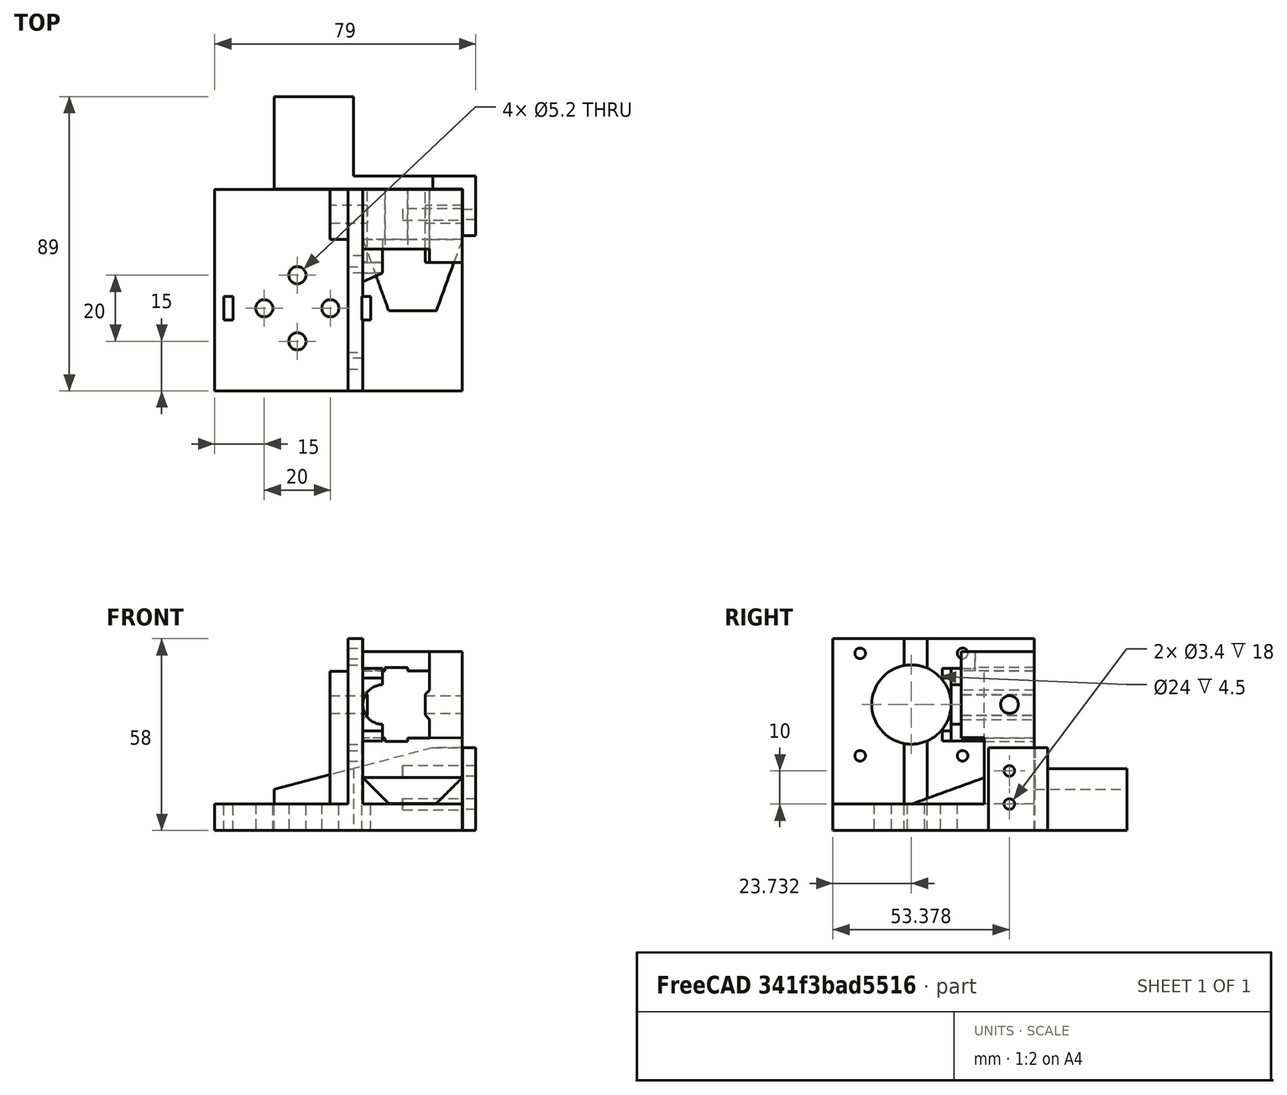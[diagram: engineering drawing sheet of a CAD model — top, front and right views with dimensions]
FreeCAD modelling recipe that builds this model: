
FCSTD DOCUMENT  (FreeCAD 1.0R39109 (Git))
Label: plotter_x_axis
License: All rights reserved
LicenseURL: https://en.wikipedia.org/wiki/All_rights_reserved
objects: Sketcher::SketchObject×20, PartDesign::Pad×17, PartDesign::Pocket×7, Mesh::Feature×2, PartDesign::Body×2, PartDesign::LinearPattern×1
note: 116 computed .brp shape members not serialized (recipe doc carries the construction recipe); baked Part::Feature solids carry a one-line shape summary decoded from their .brp

FEATURE [Mesh::Feature] _0x20_v_slot  label="20x20_v-slot"
  Placement = pos=(29.9,14,38) rot=(0,0,1;0rad)
FEATURE [Mesh::Feature] Motor_NEMA17
  Placement = pos=(-1.8,-1.5,38) rot=(0,1,0;1.5708rad)
FEATURE [Sketcher::SketchObject] Sketch007
  ArcFitTolerance = 1e-06
  AttachmentSupport = -> [XY_Plane001]
  FullyConstrained = false
  MakeInternals = false
  MapMode = 5
  sketch-geometry (19):
    g0: LineSegment StartX=49.9144 StartY=35.9499 StartZ=0 EndX=-25 EndY=35.9499 EndZ=0
    g1: LineSegment StartX=-25 StartY=35.9499 StartZ=0 EndX=-25 EndY=-25 EndZ=0
    g2: LineSegment StartX=-25 StartY=-25 StartZ=0 EndX=49.9144 EndY=-25 EndZ=0
    g3: LineSegment StartX=49.9144 StartY=-25 StartZ=0 EndX=49.9144 EndY=35.9499 EndZ=0
    g4: Circle CenterX=0 CenterY=10 CenterZ=0 NormalX=0 NormalY=0 NormalZ=1 AngleXU=0 Radius=2.6
    g5: Circle CenterX=10 CenterY=0 CenterZ=0 NormalX=0 NormalY=0 NormalZ=1 AngleXU=0 Radius=2.6
    g6: Circle CenterX=-10 CenterY=0 CenterZ=0 NormalX=0 NormalY=0 NormalZ=1 AngleXU=0 Radius=2.6
    g7: Circle CenterX=0 CenterY=-10 CenterZ=0 NormalX=0 NormalY=0 NormalZ=1 AngleXU=0 Radius=2.6
    g8: LineSegment [constr] StartX=43.4104 StartY=34.4675 StartZ=0 EndX=43.4104 EndY=14.8633 EndZ=0
    g9: LineSegment StartX=22.25 StartY=-3.5 StartZ=0 EndX=22.25 EndY=3.5 EndZ=0
    g10: LineSegment StartX=22.25 StartY=3.5 StartZ=0 EndX=19.5 EndY=3.5 EndZ=0
    g11: LineSegment StartX=19.5 StartY=3.5 StartZ=0 EndX=19.5 EndY=-3.5 EndZ=0
    g12: LineSegment StartX=19.5 StartY=-3.5 StartZ=0 EndX=22.25 EndY=-3.5 EndZ=0
    g13: GeomPoint [constr] X=20.875 Y=0 Z=0
    g14: LineSegment StartX=-19.5 StartY=-3.5 StartZ=0 EndX=-19.5 EndY=3.5 EndZ=0
    g15: LineSegment StartX=-19.5 StartY=3.5 StartZ=0 EndX=-22.25 EndY=3.5 EndZ=0
    g16: LineSegment StartX=-22.25 StartY=3.5 StartZ=0 EndX=-22.25 EndY=-3.5 EndZ=0
    g17: LineSegment StartX=-22.25 StartY=-3.5 StartZ=0 EndX=-19.5 EndY=-3.5 EndZ=0
    g18: GeomPoint [constr] X=-20.875 Y=0 Z=0
  constraints (49):
    c: Coincident(g0,g1)
    c: Coincident(g1,g2)
    c: Coincident(g2,g3)
    c: Coincident(g3,g0)
    c: Horizontal(g0)
    c: Horizontal(g2)
    c: Vertical(g1)
    c: Vertical(g3)
    c: Diameter(g4) = 5.2
    c: PointOnObject(g4,g-2)
    c: Diameter(g5) = 5.2
    c: PointOnObject(g5,g-1)
    c: Diameter(g6) = 5.2
    c: Diameter(g7) = 5.2
    c: PointOnObject(g7,g-2)
    c: DistanceX(g-1,g5) = 10
    c: DistanceY(g7,g-1) = 10
    c: DistanceY(g-1,g4) = 10
    c: DistanceX(g6,g-1) = 10
    c: PointOnObject(g6,g-1)
    c: Vertical(g8)
    c: DistanceY(g1,g-1) = 25
    c: DistanceX(g1,g-1) = 25
    c: Coincident(g9,g10)
    c: Coincident(g10,g11)
    c: Coincident(g11,g12)
    c: Coincident(g12,g9)
    c: Vertical(g9)
    c: Vertical(g11)
    c: Horizontal(g10)
    c: Horizontal(g12)
    c: Symmetric(g11,g9,g13)
    c: PointOnObject(g13,g-1)
    c: Coincident(g14,g15)
    c: Coincident(g15,g16)
    c: Coincident(g16,g17)
    c: Coincident(g17,g14)
    c: Vertical(g14)
    c: Vertical(g16)
    c: Horizontal(g15)
    c: Horizontal(g17)
    c: Symmetric(g16,g14,g18)
    c: PointOnObject(g18,g-1)
    c: Equal(g11,g14)
    c: DistanceY(g11,g11) = 7
    c: Equal(g10,g15)
    c: DistanceX(g15,g15) = 2.75
    c: DistanceX(g14,g11) = 39
    c: DistanceX(g14,g-1) = 19.5
FEATURE [PartDesign::Pad] Pad005
  Direction = (0,0,1)
  Length = 8
  Length2 = 10
  Profile = -> Sketch007
  ReferenceAxis = -> Sketch007 [N_Axis]
  Refine = true
  Suppressed = false
  Type = 0
FEATURE [Sketcher::SketchObject] Sketch009
  ArcFitTolerance = 1e-06
  AttachmentSupport = -> [Pad005]
  ExternalGeometry = -> [Pad005]
  FullyConstrained = false
  MakeInternals = false
  MapMode = 5
  Placement = pos=(0,0,8) rot=(0,0,1;0rad)
  sketch-geometry (4):
    g0: LineSegment StartX=49.9144 StartY=35.9499 StartZ=0 EndX=9.91437 EndY=35.9499 EndZ=0
    g1: LineSegment StartX=9.91437 StartY=35.9499 StartZ=0 EndX=9.91437 EndY=20.8055 EndZ=0
    g2: LineSegment StartX=9.91437 StartY=20.8055 StartZ=0 EndX=49.9144 EndY=20.8055 EndZ=0
    g3: LineSegment StartX=49.9144 StartY=20.8055 StartZ=0 EndX=49.9144 EndY=35.9499 EndZ=0
  constraints (10):
    c: Coincident(g0,g1)
    c: Coincident(g1,g2)
    c: Coincident(g2,g3)
    c: Coincident(g3,g0)
    c: Horizontal(g0)
    c: Horizontal(g2)
    c: Vertical(g1)
    c: Vertical(g3)
    c: Distance(g1,g3) = 40
    c: Coincident(g0,g-4)
FEATURE [PartDesign::Pad] Pad006
  BaseFeature = -> Pad005
  Direction = (0,0,1)
  Length = 40.1
  Length2 = 10
  Profile = -> Sketch009
  ReferenceAxis = -> Sketch009 [N_Axis]
  Refine = true
  Suppressed = false
  Type = 0
FEATURE [Sketcher::SketchObject] Sketch010
  ArcFitTolerance = 1e-06
  AttachmentSupport = -> [Pad006]
  ExternalGeometry = -> [Pad006]
  FullyConstrained = false
  MakeInternals = false
  MapMode = 5
  Placement = pos=(0,20.8055,0) rot=(1,0,0;1.5708rad)
  sketch-geometry (17):
    g0: LineSegment [constr] StartX=29.9144 StartY=48.1 StartZ=0 EndX=29.9144 EndY=14.8286 EndZ=0
    g1: LineSegment StartX=19.8144 StartY=48.1 StartZ=0 EndX=19.8144 EndY=42.4266 EndZ=0
    g2: LineSegment StartX=19.8144 StartY=42.4266 StartZ=0 EndX=21.1404 EndY=41.0594 EndZ=0
    g3: LineSegment StartX=21.1404 StartY=41.0594 StartZ=0 EndX=21.1404 EndY=34.8594 EndZ=0
    g4: LineSegment StartX=21.1404 StartY=34.8594 StartZ=0 EndX=19.8144 EndY=33.5734 EndZ=0
    g5: LineSegment StartX=19.8144 StartY=33.5734 StartZ=0 EndX=19.8144 EndY=27.9 EndZ=0
    g6: LineSegment StartX=19.8144 StartY=27.9 StartZ=0 EndX=26.496 EndY=27.9 EndZ=0
    g7: LineSegment StartX=26.496 StartY=27.9 StartZ=0 EndX=26.496 EndY=26.9 EndZ=0
    g8: LineSegment StartX=26.496 StartY=26.9 StartZ=0 EndX=33.3327 EndY=26.9 EndZ=0
    g9: LineSegment StartX=33.3327 StartY=26.9 StartZ=0 EndX=33.3327 EndY=27.9 EndZ=0
    g10: LineSegment StartX=33.3327 StartY=27.9 StartZ=0 EndX=40.0144 EndY=27.9 EndZ=0
    g11: LineSegment StartX=40.0144 StartY=27.9 StartZ=0 EndX=40.0144 EndY=33.5734 EndZ=0
    g12: LineSegment StartX=40.0144 StartY=33.5734 StartZ=0 EndX=38.6893 EndY=34.9653 EndZ=0
    g13: LineSegment StartX=38.6893 StartY=34.9653 StartZ=0 EndX=38.6893 EndY=41.1653 EndZ=0
    g14: LineSegment StartX=38.6893 StartY=41.1653 StartZ=0 EndX=40.0144 EndY=42.4266 EndZ=0
    g15: LineSegment StartX=40.0144 StartY=42.4266 StartZ=0 EndX=40.0144 EndY=48.1 EndZ=0
    g16: LineSegment StartX=40.0144 StartY=48.1 StartZ=0 EndX=19.8144 EndY=48.1 EndZ=0
  constraints (46):
    c: Symmetric(g-3,g-3,g0)
    c: Vertical(g0)
    c: PointOnObject(g1,g-3)
    c: Vertical(g1)
    c: Coincident(g1,g2)
    c: Coincident(g2,g3)
    c: Vertical(g3)
    c: Coincident(g3,g4)
    c: Coincident(g4,g5)
    c: Vertical(g5)
    c: Coincident(g5,g6)
    c: Coincident(g6,g7)
    c: Vertical(g7)
    c: Coincident(g7,g8)
    c: Horizontal(g8)
    c: Coincident(g8,g9)
    c: Vertical(g9)
    c: Coincident(g9,g10)
    c: Coincident(g10,g11)
    c: Vertical(g11)
    c: Coincident(g11,g12)
    c: Coincident(g12,g13)
    c: Vertical(g13)
    c: Coincident(g13,g14)
    c: Coincident(g14,g15)
    c: PointOnObject(g15,g-3)
    c: Vertical(g15)
    c: Coincident(g15,g16)
    c: Coincident(g16,g1)
    c: Equal(g13,g3)
    c: Equal(g15,g1)
    c: Equal(g1,g5)
    c: Equal(g5,g11)
    c: Equal(g6,g10)
    c: Equal(g9,g7)
    c: DistanceY(g3,g3) = 6.2
    c: DistanceX(g4,g11) = 20.2
    c: DistanceX(g11,g14) = 0
    c: DistanceX(g1,g4) = 0
    c: DistanceY(g10,g15) = 20.2
    c: DistanceY(g10,g5) = 0
    c: Parallel(g6,g10)
    c: DistanceY(g9,g9) = 1
    c: DistanceX(g1,g0) = 10.1
    c: Perpendicular(g4,g2)
    c: Perpendicular(g12,g14)
FEATURE [PartDesign::Pocket] Pocket004
  BaseFeature = -> Pad006
  Direction = (0,1,-2e-16)
  Length = 50
  Length2 = 5
  Profile = -> Sketch010
  ReferenceAxis = -> Sketch010 [N_Axis]
  Refine = true
  Suppressed = false
  Type = 0
FEATURE [Sketcher::SketchObject] Sketch011
  ArcFitTolerance = 1e-06
  AttachmentSupport = -> [Pocket004]
  ExternalGeometry = -> [Pocket004]
  FullyConstrained = true
  MakeInternals = false
  MapMode = 5
  Placement = pos=(0,0,8) rot=(0,0,1;0rad)
  sketch-geometry (8):
    g0: LineSegment StartX=15.3144 StartY=20.8055 StartZ=0 EndX=15.3144 EndY=-25 EndZ=0
    g1: LineSegment StartX=15.3144 StartY=-25 StartZ=0 EndX=19.8144 EndY=-25 EndZ=0
    g2: LineSegment StartX=19.8144 StartY=-25 StartZ=0 EndX=19.8144 EndY=-3.5 EndZ=0
    g3: LineSegment StartX=19.8144 StartY=-3.5 StartZ=0 EndX=19.5 EndY=-3.5 EndZ=0
    g4: LineSegment StartX=19.5 StartY=-3.5 StartZ=0 EndX=19.5 EndY=3.5 EndZ=0
    g5: LineSegment StartX=19.5 StartY=3.5 StartZ=0 EndX=19.8144 EndY=3.5 EndZ=0
    g6: LineSegment StartX=19.8144 StartY=3.5 StartZ=0 EndX=19.8144 EndY=20.8055 EndZ=0
    g7: LineSegment StartX=19.8144 StartY=20.8055 StartZ=0 EndX=15.3144 EndY=20.8055 EndZ=0
  constraints (21):
    c: Vertical(g0)
    c: Coincident(g0,g1)
    c: Coincident(g1,g2)
    c: Vertical(g2)
    c: Coincident(g2,g3)
    c: Coincident(g3,g4)
    c: Coincident(g4,g5)
    c: Horizontal(g5)
    c: Coincident(g5,g6)
    c: Vertical(g6)
    c: Coincident(g6,g7)
    c: Coincident(g7,g0)
    c: Coincident(g4,g-3)
    c: Coincident(g3,g-4)
    c: Parallel(g3,g-1)
    c: Equal(g1,g7)
    c: Parallel(g7,g1)
    c: PointOnObject(g1,g-6)
    c: Coincident(g6,g-5)
    c: DistanceY(g0,g-5) = 0
    c: DistanceX(g1,g1) = 4.5
FEATURE [PartDesign::Pad] Pad007
  BaseFeature = -> Pocket004
  Direction = (0,0,1)
  Length = 50
  Length2 = 10
  Profile = -> Sketch011
  ReferenceAxis = -> Sketch011 [N_Axis]
  Refine = true
  Suppressed = false
  Type = 0
FEATURE [Sketcher::SketchObject] Sketch012
  ArcFitTolerance = 1e-06
  AttachmentSupport = -> [Pad007]
  ExternalGeometry = -> [Pad007]
  FullyConstrained = false
  MakeInternals = false
  MapMode = 5
  Placement = pos=(49.9144,0,0) rot=(0.57735,0.57735,0.57735;2.0944rad)
  sketch-geometry (1):
    g0: Circle CenterX=28.4297 CenterY=38.1 CenterZ=0 NormalX=0 NormalY=0 NormalZ=1 AngleXU=0 Radius=2.7
  constraints (2):
    c: Diameter(g0) = 5.4
    c: DistanceY(g0,g-3) = 10
FEATURE [Sketcher::SketchObject] Sketch013
  ArcFitTolerance = 1e-06
  AttachmentSupport = -> [Pad007]
  ExternalGeometry = -> [Pad007]
  FullyConstrained = true
  MakeInternals = false
  MapMode = 5
  Placement = pos=(0,20.8055,0) rot=(1,0,0;1.5708rad)
  sketch-geometry (8):
    g0: LineSegment StartX=40.0144 StartY=48.1 StartZ=0 EndX=40.0144 EndY=42.4266 EndZ=0
    g1: LineSegment StartX=40.0144 StartY=42.4266 StartZ=0 EndX=38.6893 EndY=41.1653 EndZ=0
    g2: LineSegment StartX=38.6893 StartY=41.1653 StartZ=0 EndX=38.6893 EndY=34.9653 EndZ=0
    g3: LineSegment StartX=38.6893 StartY=34.9653 StartZ=0 EndX=40.0144 EndY=33.5734 EndZ=0
    g4: LineSegment StartX=40.0144 StartY=33.5734 StartZ=0 EndX=40.0144 EndY=27.9 EndZ=0
    g5: LineSegment StartX=40.0144 StartY=27.9 StartZ=0 EndX=49.9144 EndY=28.05 EndZ=0
    g6: LineSegment StartX=49.9144 StartY=28.05 StartZ=0 EndX=49.9144 EndY=48.1 EndZ=0
    g7: LineSegment StartX=49.9144 StartY=48.1 StartZ=0 EndX=40.0144 EndY=48.1 EndZ=0
  constraints (16):
    c: Coincident(g-4,g0)
    c: Coincident(g0,g-5)
    c: Coincident(g0,g1)
    c: Coincident(g1,g-6)
    c: Coincident(g1,g2)
    c: Coincident(g2,g-7)
    c: Coincident(g2,g3)
    c: Coincident(g3,g-8)
    c: Coincident(g3,g4)
    c: Coincident(g4,g-8)
    c: Coincident(g4,g5)
    c: Symmetric(g-9,g-9,g5)
    c: Coincident(g5,g6)
    c: Coincident(g6,g-9)
    c: Coincident(g6,g7)
    c: Coincident(g7,g0)
FEATURE [PartDesign::Pad] Pad008
  BaseFeature = -> Pad007
  Direction = (0,-1,2e-16)
  Length = 7
  Length2 = 10
  Profile = -> Sketch013
  ReferenceAxis = -> Sketch013 [N_Axis]
  Refine = true
  Suppressed = false
  Type = 0
FEATURE [PartDesign::Pad] Pad009
  BaseFeature = -> Pad008
  Direction = (0,-1,0)
  Length = 7
  Length2 = 10
  Profile = -> Pad008 [Face35]
  Refine = true
  Suppressed = false
  Type = 0
FEATURE [PartDesign::Pocket] Pocket005
  BaseFeature = -> Pad009
  Direction = (-1,0,0)
  Length = 1000
  Length2 = 5
  Profile = -> Sketch012
  ReferenceAxis = -> Sketch012 [N_Axis]
  Refine = true
  Suppressed = false
  Type = 0
FEATURE [Sketcher::SketchObject] Sketch014
  ArcFitTolerance = 1e-06
  AttachmentSupport = -> [Pocket005]
  ExternalGeometry = -> [Pocket005]
  FullyConstrained = false
  MakeInternals = false
  MapMode = 5
  Placement = pos=(19.8144,0,0) rot=(0.57735,0.57735,0.57735;2.0944rad)
  sketch-geometry (10):
    g0: Circle CenterX=-1.26785 CenterY=38.1 CenterZ=0 NormalX=0 NormalY=0 NormalZ=1 AngleXU=0 Radius=12
    g1: LineSegment [constr] StartX=14.2321 StartY=22.6 StartZ=0 EndX=14.2321 EndY=53.6 EndZ=0
    g2: LineSegment [constr] StartX=14.2321 StartY=53.6 StartZ=0 EndX=-16.7679 EndY=53.6 EndZ=0
    g3: LineSegment [constr] StartX=-16.7679 StartY=53.6 StartZ=0 EndX=-16.7679 EndY=22.6 EndZ=0
    g4: LineSegment [constr] StartX=-16.7679 StartY=22.6 StartZ=0 EndX=14.2321 EndY=22.6 EndZ=0
    g5: GeomPoint [constr] X=-1.26785 Y=38.1 Z=0
    g6: Circle CenterX=-16.7679 CenterY=53.6 CenterZ=0 NormalX=0 NormalY=0 NormalZ=1 AngleXU=0 Radius=1.6
    g7: Circle CenterX=14.2321 CenterY=53.6 CenterZ=0 NormalX=0 NormalY=0 NormalZ=1 AngleXU=0 Radius=1.6
    g8: Circle CenterX=14.2321 CenterY=22.6 CenterZ=0 NormalX=0 NormalY=0 NormalZ=1 AngleXU=0 Radius=1.6
    g9: Circle CenterX=-16.7679 CenterY=22.6 CenterZ=0 NormalX=0 NormalY=0 NormalZ=1 AngleXU=0 Radius=1.6
  constraints (22):
    c: Diameter(g0) = 24
    c: Coincident(g1,g2)
    c: Coincident(g2,g3)
    c: Coincident(g3,g4)
    c: Coincident(g4,g1)
    c: Vertical(g1)
    c: Vertical(g3)
    c: Horizontal(g2)
    c: Horizontal(g4)
    c: Symmetric(g3,g1,g5)
    c: Coincident(g5,g0)
    c: Equal(g2,g3)
    c: DistanceX(g2,g2) = 31
    c: Coincident(g6,g2)
    c: Coincident(g7,g1)
    c: Coincident(g8,g1)
    c: Coincident(g9,g3)
    c: Diameter(g9) = 3.2
    c: Equal(g9,g6)
    c: Equal(g6,g7)
    c: Equal(g7,g8)
    c: DistanceY(g0,g-3) = 10
FEATURE [PartDesign::Pocket] Pocket006
  BaseFeature = -> Pocket005
  Direction = (-1,0,0)
  Length = 5
  Length2 = 5
  Profile = -> Sketch014
  ReferenceAxis = -> Sketch014 [N_Axis]
  Refine = true
  Suppressed = false
  Type = 0
FEATURE [Sketcher::SketchObject] Sketch015
  ArcFitTolerance = 1e-06
  AttachmentSupport = -> [Pocket006]
  ExternalGeometry = -> [Pocket006,Sketch007]
  FullyConstrained = true
  MakeInternals = false
  MapMode = 5
  Placement = pos=(0,20.8055,0) rot=(1,0,0;1.5708rad)
  sketch-geometry (7):
    g0: GeomPoint [constr] X=34.8644 Y=8 Z=0
    g1: GeomPoint X=34.8644 Y=8 Z=0
    g2: LineSegment StartX=19.8144 StartY=16 StartZ=0 EndX=19.8144 EndY=0 EndZ=0
    g3: LineSegment StartX=19.8144 StartY=0 StartZ=0 EndX=49.9144 EndY=0 EndZ=0
    g4: LineSegment StartX=49.9144 StartY=0 StartZ=0 EndX=49.9144 EndY=16 EndZ=0
    g5: LineSegment StartX=49.9144 StartY=16 StartZ=0 EndX=19.8144 EndY=16 EndZ=0
    g6: GeomPoint [constr] X=34.8644 Y=8 Z=0
  constraints (13):
    c: Symmetric(g-4,g-4,g0)
    c: Coincident(g1,g0)
    c: Coincident(g2,g3)
    c: Coincident(g3,g4)
    c: Coincident(g4,g5)
    c: Coincident(g5,g2)
    c: Vertical(g2)
    c: Vertical(g4)
    c: Horizontal(g3)
    c: Horizontal(g5)
    c: Symmetric(g4,g2,g6)
    c: Symmetric(g-4,g-4,g6)
    c: Coincident(g3,g-6)
FEATURE [PartDesign::Pad] Pad010
  BaseFeature = -> Pocket006
  Direction = (0,-1,2e-16)
  Length = 21.5
  Length2 = 10
  Profile = -> Sketch015
  ReferenceAxis = -> Sketch015 [N_Axis]
  Refine = true
  Suppressed = false
  TaperAngle = -20
  Type = 0
FEATURE [PartDesign::Pad] Pad011
  BaseFeature = -> Pad010
  Direction = (0,1,0)
  Length = 16
  Length2 = 10
  Profile = -> Pad010 [Face47]
  Refine = true
  Suppressed = false
  Type = 0
FEATURE [PartDesign::Pocket] Pocket007
  BaseFeature = -> Pad011
  Direction = (0,0,1)
  Length = 20
  Length2 = 5
  Profile = -> Pad011 [Face21]
  Refine = true
  Suppressed = false
  Type = 0
FEATURE [Sketcher::SketchObject] Sketch016
  ArcFitTolerance = 1e-06
  AttachmentSupport = -> [Pocket007]
  ExternalGeometry = -> [Pocket007]
  FullyConstrained = true
  MakeInternals = false
  MapMode = 5
  Placement = pos=(49.9144,0,0) rot=(0.57735,0.57735,0.57735;2.0944rad)
  sketch-geometry (2):
    g0: Circle CenterX=28.3777 CenterY=8 CenterZ=0 NormalX=0 NormalY=0 NormalZ=1 AngleXU=0 Radius=1.7
    g1: GeomPoint X=35.9499 Y=8 Z=0
  constraints (5):
    c: PointOnObject(g1,g-3)
    c: DistanceY(g1,g-4) = 0
    c: Symmetric(g-4,g1,g0)
    c: Diameter(g0) = 3.4
    c: DistanceY(g-1,g-4) = 8
FEATURE [PartDesign::Pocket] Pocket008
  BaseFeature = -> Pocket007
  Direction = (-1,0,0)
  Length = 18
  Length2 = 5
  Profile = -> Sketch016
  ReferenceAxis = -> Sketch016 [N_Axis]
  Refine = true
  Suppressed = false
  Type = 0
FEATURE [PartDesign::LinearPattern] LinearPattern
  BaseFeature = -> Pocket008
  Direction = -> Sketch016 [V_Axis]
  Length = 10
  Mode = 0
  Occurrences = 2
  Offset = 10
  Originals = -> [Pocket008]
  Refine = true
  Suppressed = false
  TransformMode = 0
FEATURE [Sketcher::SketchObject] Sketch017
  ArcFitTolerance = 1e-06
  AttachmentSupport = -> [YZ_Plane002]
  FullyConstrained = true
  MakeInternals = false
  MapMode = 5
  Placement = pos=(0,0,0) rot=(0.57735,0.57735,0.57735;2.0944rad)
  sketch-geometry (6):
    g0: LineSegment StartX=22 StartY=25 StartZ=0 EndX=22 EndY=0 EndZ=0
    g1: LineSegment StartX=22 StartY=0 StartZ=0 EndX=40 EndY=0 EndZ=0
    g2: LineSegment StartX=40 StartY=0 StartZ=0 EndX=40 EndY=25 EndZ=0
    g3: LineSegment StartX=40 StartY=25 StartZ=0 EndX=22 EndY=25 EndZ=0
    g4: Circle CenterX=28.38 CenterY=8 CenterZ=0 NormalX=0 NormalY=0 NormalZ=1 AngleXU=0 Radius=1.6
    g5: Circle CenterX=28.38 CenterY=18 CenterZ=0 NormalX=0 NormalY=0 NormalZ=1 AngleXU=0 Radius=1.6
  constraints (18):
    c: Coincident(g0,g1)
    c: Coincident(g1,g2)
    c: Coincident(g2,g3)
    c: Coincident(g3,g0)
    c: Vertical(g0)
    c: Vertical(g2)
    c: Horizontal(g1)
    c: Horizontal(g3)
    c: Distance(g0,g2) = 18
    c: Distance(g1,g3) = 25
    c: PointOnObject(g1,g-1)
    c: DistanceX(g-1,g1) = 40
    c: Diameter(g4) = 3.2
    c: DistanceY(g1,g4) = 8
    c: DistanceX(g0,g4) = 6.38
    c: Diameter(g5) = 3.2
    c: DistanceX(g5,g4) = 0
    c: DistanceY(g4,g5) = 10
FEATURE [PartDesign::Pad] Pad012
  Direction = (1,0,0)
  Length = 4
  Length2 = 10
  Placement = pos=(0,0,0) rot=(1,1,1;2.0944rad)
  Profile = -> Sketch017
  ReferenceAxis = -> Sketch017 [N_Axis]
  Refine = true
  Suppressed = false
  Type = 0
FEATURE [Sketcher::SketchObject] Sketch018
  ArcFitTolerance = 1e-06
  AttachmentSupport = -> [Pad012]
  ExternalGeometry = -> [Pad012]
  FullyConstrained = true
  MakeInternals = false
  MapMode = 5
  Placement = pos=(0,0,0) rot=(0.57735,0.57735,-0.57735;4.18879rad)
  sketch-geometry (4):
    g0: LineSegment StartX=40 StartY=1.33e-14 StartZ=0 EndX=36.1 EndY=1.33e-14 EndZ=0
    g1: LineSegment StartX=36.1 StartY=1.33e-14 StartZ=0 EndX=36.1 EndY=-25 EndZ=0
    g2: LineSegment StartX=36.1 StartY=-25 StartZ=0 EndX=40 EndY=-25 EndZ=0
    g3: LineSegment StartX=40 StartY=-25 StartZ=0 EndX=40 EndY=1.42e-14 EndZ=0
  constraints (11):
    c: Coincident(g0,g1)
    c: Coincident(g1,g2)
    c: Coincident(g2,g3)
    c: Coincident(g3,g0)
    c: Horizontal(g0)
    c: Horizontal(g2)
    c: Vertical(g1)
    c: Vertical(g3)
    c: Distance(g1,g3) = 3.9
    c: Distance(g0,g2) = 25
    c: Coincident(g0,g-4)
FEATURE [PartDesign::Pad] Pad013
  BaseFeature = -> Pad012
  Direction = (-1,0,0)
  Length = 57
  Length2 = 10
  Placement = pos=(0,0,0) rot=(1,1,1;2.0944rad)
  Profile = -> Sketch018
  ReferenceAxis = -> Sketch018 [N_Axis]
  Refine = true
  Suppressed = false
  Type = 0
FEATURE [Sketcher::SketchObject] Sketch019
  ArcFitTolerance = 1e-06
  AttachmentSupport = -> [Pad013]
  ExternalGeometry = -> [Pad013]
  FullyConstrained = true
  MakeInternals = false
  MapMode = 5
  Placement = pos=(9.6e-15,40,0) rot=(0.57735,0.57735,0.57735;4.18879rad)
  sketch-geometry (3):
    g0: LineSegment StartX=25 StartY=-9 StartZ=0 EndX=12.5 EndY=-57 EndZ=0
    g1: LineSegment StartX=12.5 StartY=-57 StartZ=0 EndX=25 EndY=-57 EndZ=0
    g2: LineSegment StartX=25 StartY=-57 StartZ=0 EndX=25 EndY=-9 EndZ=0
  constraints (7):
    c: PointOnObject(g0,g-3)
    c: Symmetric(g-4,g-4,g0)
    c: Coincident(g0,g1)
    c: Coincident(g1,g-4)
    c: Coincident(g1,g2)
    c: Coincident(g2,g0)
    c: DistanceY(g2,g2) = 48
FEATURE [PartDesign::Pocket] Pocket009
  BaseFeature = -> Pad013
  Direction = (0,-1,0)
  Length = 5
  Length2 = 5
  Placement = pos=(0,0,0) rot=(1,1,1;2.0944rad)
  Profile = -> Sketch019
  ReferenceAxis = -> Sketch019 [N_Axis]
  Refine = true
  Suppressed = false
  Type = 0
FEATURE [Sketcher::SketchObject] Sketch020
  ArcFitTolerance = 1e-06
  AttachmentSupport = -> [Pocket009]
  ExternalGeometry = -> [Pocket009]
  FullyConstrained = true
  MakeInternals = false
  MapMode = 5
  Placement = pos=(9.6e-15,40,0) rot=(0.57735,0.57735,0.57735;4.18879rad)
  sketch-geometry (4):
    g0: LineSegment StartX=0 StartY=-57 StartZ=0 EndX=12.5 EndY=-57 EndZ=0
    g1: LineSegment StartX=12.5 StartY=-57 StartZ=0 EndX=18.75 EndY=-33 EndZ=0
    g2: LineSegment StartX=18.75 StartY=-33 StartZ=0 EndX=0 EndY=-33 EndZ=0
    g3: LineSegment StartX=0 StartY=-33 StartZ=0 EndX=0 EndY=-57 EndZ=0
  constraints (9):
    c: Coincident(g-5,g0)
    c: Coincident(g0,g-4)
    c: Coincident(g0,g1)
    c: Symmetric(g-3,g-3,g1)
    c: Coincident(g1,g2)
    c: PointOnObject(g2,g-5)
    c: Horizontal(g2)
    c: Coincident(g2,g3)
    c: Coincident(g3,g0)
FEATURE [PartDesign::Pad] Pad014
  BaseFeature = -> Pocket009
  Direction = (0,1,0)
  Length = 24
  Length2 = 10
  Placement = pos=(0,0,0) rot=(1,1,1;2.0944rad)
  Profile = -> Sketch020
  ReferenceAxis = -> Sketch020 [N_Axis]
  Refine = true
  Suppressed = false
  Type = 0
FEATURE [PartDesign::Body] Body002  label="limittrigger"
  AllowCompound = false
  Group = -> [Sketch017,Pad012,Sketch018,Pad013,Sketch019,Pocket009,Sketch020,Pad014]
  Origin = -> Origin002
  Placement = pos=(50,0,0) rot=(0,0,1;0rad)
  Tip = -> Pad014
FEATURE [Sketcher::SketchObject] Sketch021
  ArcFitTolerance = 1e-06
  AttachmentSupport = -> [LinearPattern]
  ExternalGeometry = -> [LinearPattern]
  FullyConstrained = false
  MakeInternals = false
  MapMode = 5
  Placement = pos=(19.8144,-2.5251e-12,7.02e-13) rot=(0.57735,0.57735,0.57735;2.0944rad)
  sketch-geometry (5):
    g0: LineSegment StartX=10.7321 StartY=38.1 StartZ=0 EndX=10.7321 EndY=49.1 EndZ=0
    g1: LineSegment StartX=10.7321 StartY=49.1 StartZ=0 EndX=13.8055 EndY=49.1 EndZ=0
    g2: LineSegment StartX=13.8055 StartY=49.1 StartZ=0 EndX=13.8055 EndY=27.1 EndZ=0
    g3: LineSegment StartX=13.8055 StartY=27.1 StartZ=0 EndX=10.7321 EndY=27.1 EndZ=0
    g4: LineSegment StartX=10.7321 StartY=27.1 StartZ=0 EndX=10.7321 EndY=38.1 EndZ=0
  constraints (13):
    c: Coincident(g-4,g0)
    c: Coincident(g0,g1)
    c: Horizontal(g1)
    c: Coincident(g1,g2)
    c: Vertical(g2)
    c: Coincident(g2,g3)
    c: Horizontal(g3)
    c: Coincident(g3,g4)
    c: Coincident(g4,g0)
    c: Tangent(g4,g-3)
    c: PointOnObject(g2,g-5)
    c: DistanceY(g2,g2) = 22
    c: Equal(g4,g0)
FEATURE [PartDesign::Pad] Pad015  label="ExtrusionRest"
  BaseFeature = -> LinearPattern
  Direction = (1,-1.275e-13,3.55e-14)
  Length = 6
  Length2 = 10
  Profile = -> Sketch021
  ReferenceAxis = -> Sketch021 [N_Axis]
  Refine = true
  Suppressed = false
  Type = 0
FEATURE [Sketcher::SketchObject] Sketch025
  ArcFitTolerance = 1e-06
  AttachmentSupport = -> [Pad015]
  ExternalGeometry = -> [Pad015]
  FullyConstrained = false
  MakeInternals = false
  MapMode = 5
  Placement = pos=(-9.629e-13,0,27.1) rot=(1,0,0;3.14159rad)
  sketch-geometry (3):
    g0: LineSegment StartX=25.8144 StartY=-10.7321 StartZ=0 EndX=19.8144 EndY=-10.7321 EndZ=0
    g1: LineSegment StartX=25.8144 StartY=-10.7321 StartZ=0 EndX=19.8144 EndY=-8.06261 EndZ=0
    g2: LineSegment StartX=19.8144 StartY=-8.06261 StartZ=0 EndX=19.8144 EndY=-10.7321 EndZ=0
  constraints (7):
    c: Coincident(g-4,g0)
    c: Coincident(g0,g-4)
    c: Coincident(g0,g1)
    c: Coincident(g1,g2)
    c: Coincident(g2,g0)
    c: PointOnObject(g1,g-3)
    c: Angle(g-3) = -1.5708
FEATURE [PartDesign::Pad] Pad016  label="ExtrusionRestSupport"
  BaseFeature = -> Pad015
  Direction = (3.55e-14,0,-1)
  Length = 3
  Length2 = 10
  Profile = -> Sketch025
  ReferenceAxis = -> Sketch025 [N_Axis]
  Refine = true
  Reversed = true
  Suppressed = false
  Type = 0
FEATURE [Sketcher::SketchObject] Sketch026
  ArcFitTolerance = 1e-06
  AttachmentSupport = -> [Pad016]
  ExternalGeometry = -> [Pad016]
  FullyConstrained = true
  MakeInternals = false
  MapMode = 5
  Placement = pos=(-1.7445e-12,0,49.1) rot=(0,0,1;0rad)
  sketch-geometry (3):
    g0: LineSegment StartX=19.8144 StartY=10.7321 StartZ=0 EndX=25.8144 EndY=10.7321 EndZ=0
    g1: LineSegment StartX=25.8144 StartY=10.7321 StartZ=0 EndX=19.8144 EndY=8.06215 EndZ=0
    g2: LineSegment StartX=19.8144 StartY=8.06215 StartZ=0 EndX=19.8144 EndY=10.7321 EndZ=0
  constraints (7):
    c: Coincident(g-3,g0)
    c: Coincident(g0,g-3)
    c: Coincident(g0,g1)
    c: PointOnObject(g1,g-4)
    c: Coincident(g1,g2)
    c: Coincident(g2,g0)
    c: DistanceY(g2,g2) = 2.67
FEATURE [PartDesign::Pad] Pad017  label="ExtrusionRestSupport2"
  BaseFeature = -> Pad016
  Direction = (-3.55e-14,0,1)
  Length = 3
  Length2 = 10
  Profile = -> Sketch026
  ReferenceAxis = -> Sketch026 [N_Axis]
  Refine = true
  Reversed = true
  Suppressed = false
  Type = 0
FEATURE [Sketcher::SketchObject] Sketch027
  ArcFitTolerance = 1e-06
  AttachmentSupport = -> [Pad017]
  ExternalGeometry = -> [Pad017]
  FullyConstrained = true
  MakeInternals = false
  MapMode = 5
  Placement = pos=(1.3678e-12,10.7321,5.87088e-11) rot=(1,0,0;1.5708rad)
  sketch-geometry (1):
    g0: Circle CenterX=25.8144 CenterY=38.1 CenterZ=0 NormalX=0 NormalY=0 NormalZ=1 AngleXU=0 Radius=6
  constraints (2):
    c: Coincident(g0,g-5)
    c: PointOnObject(g-5,g0)
FEATURE [PartDesign::Pocket] Pocket010
  BaseFeature = -> Pad017
  Direction = (1.275e-13,1,5.4703e-12)
  Length = 3.2
  Length2 = 5
  Profile = -> Sketch027
  ReferenceAxis = -> Sketch027 [N_Axis]
  Refine = true
  Suppressed = false
  Type = 0
FEATURE [PartDesign::Pad] Pad018  label="ExtrusionCapExtension"
  BaseFeature = -> Pocket010
  Direction = (0,0,1)
  Length = 6
  Length2 = 10
  Profile = -> Pocket010 [Face26]
  Refine = true
  Suppressed = false
  Type = 0
FEATURE [Sketcher::SketchObject] Sketch028
  ArcFitTolerance = 1e-06
  AttachmentSupport = -> [Pad018]
  ExternalGeometry = -> [Pad018]
  FullyConstrained = true
  MakeInternals = false
  MapMode = 5
  Placement = pos=(0,35.9499,0) rot=(0,0.707107,0.707107;3.14159rad)
  sketch-geometry (8):
    g0: LineSegment StartX=-40.0144 StartY=48.2633 StartZ=0 EndX=-33.3327 EndY=48.2633 EndZ=0
    g1: LineSegment StartX=-33.3327 StartY=48.2633 StartZ=0 EndX=-33.3327 EndY=49.2633 EndZ=0
    g2: LineSegment StartX=-33.3327 StartY=49.2633 StartZ=0 EndX=-26.496 EndY=49.2633 EndZ=0
    g3: LineSegment StartX=-26.496 StartY=49.2633 StartZ=0 EndX=-26.496 EndY=48.2633 EndZ=0
    g4: LineSegment StartX=-26.496 StartY=48.2633 StartZ=0 EndX=-19.8144 EndY=48.2633 EndZ=0
    g5: LineSegment StartX=-19.8144 StartY=48.2633 StartZ=0 EndX=-19.8144 EndY=54.1 EndZ=0
    g6: LineSegment StartX=-19.8144 StartY=54.1 StartZ=0 EndX=-40.0144 EndY=54.1 EndZ=0
    g7: LineSegment StartX=-40.0144 StartY=54.1 StartZ=0 EndX=-40.0144 EndY=48.2633 EndZ=0
  constraints (23):
    c: Symmetric(g-4,g-4,g0)
    c: Horizontal(g0)
    c: Coincident(g0,g1)
    c: Horizontal(g2)
    c: Coincident(g2,g3)
    c: Coincident(g3,g4)
    c: PointOnObject(g4,g-3)
    c: Horizontal(g4)
    c: Coincident(g4,g5)
    c: PointOnObject(g5,g-3)
    c: Coincident(g5,g6)
    c: Coincident(g6,g-4)
    c: Horizontal(g6)
    c: Coincident(g7,g6)
    c: Coincident(g7,g0)
    c: DistanceY(g3,g0) = 0
    c: Equal(g4,g0)
    c: Coincident(g1,g2)
    c: Parallel(g1,g7)
    c: Parallel(g3,g1)
    c: DistanceY(g-10,g-10) = 1
    c: Equal(g-10,g3)
    c: Equal(g-11,g2)
FEATURE [PartDesign::Pad] Pad  label="ExtrusionCap"
  BaseFeature = -> Pad018
  Direction = (0,1,-2e-16)
  Length = 18
  Length2 = 10
  Profile = -> Sketch028
  ReferenceAxis = -> Sketch028 [N_Axis]
  Refine = true
  Reversed = true
  Suppressed = false
  Type = 0
FEATURE [Sketcher::SketchObject] Sketch
  ArcFitTolerance = 1e-06
  AttachmentSupport = -> [Pad]
  ExternalGeometry = -> [Pad]
  FullyConstrained = true
  MakeInternals = false
  MapMode = 5
  Placement = pos=(0,17.9499,0) rot=(1,0,0;1.5708rad)
  sketch-geometry (4):
    g0: LineSegment StartX=25.8144 StartY=49.1 StartZ=0 EndX=19.8144 EndY=49.1 EndZ=0
    g1: LineSegment StartX=19.8144 StartY=49.1 StartZ=0 EndX=19.8144 EndY=48.2633 EndZ=0
    g2: LineSegment StartX=19.8144 StartY=48.2633 StartZ=0 EndX=25.8144 EndY=48.2633 EndZ=0
    g3: LineSegment StartX=25.8144 StartY=48.2633 StartZ=0 EndX=25.8144 EndY=49.1 EndZ=0
  constraints (10):
    c: Coincident(g0,g1)
    c: Coincident(g1,g2)
    c: Coincident(g2,g3)
    c: Coincident(g3,g0)
    c: Horizontal(g0)
    c: Horizontal(g2)
    c: Vertical(g1)
    c: Vertical(g3)
    c: Coincident(g0,g-6)
    c: Coincident(g1,g-4)
FEATURE [PartDesign::Pad] Pad019
  BaseFeature = -> Pad
  Direction = (0,-1,2e-16)
  Length = 7
  Length2 = 10
  Profile = -> Sketch
  ReferenceAxis = -> Sketch [N_Axis]
  Refine = true
  Suppressed = false
  Type = 0
FEATURE [Sketcher::SketchObject] Sketch029
  ArcFitTolerance = 1e-06
  AttachmentSupport = -> [Pad019]
  ExternalGeometry = -> [Pad019]
  FullyConstrained = true
  MakeInternals = false
  MapMode = 5
  Placement = pos=(0,20.8055,0) rot=(1,0,0;1.5708rad)
  sketch-geometry (4):
    g0: LineSegment StartX=25.8144 StartY=27.1 StartZ=0 EndX=25.8144 EndY=27.9 EndZ=0
    g1: LineSegment StartX=25.8144 StartY=27.9 StartZ=0 EndX=19.8144 EndY=27.9 EndZ=0
    g2: LineSegment StartX=19.8144 StartY=27.9 StartZ=0 EndX=19.8144 EndY=27.1 EndZ=0
    g3: LineSegment StartX=19.8144 StartY=27.1 StartZ=0 EndX=25.8144 EndY=27.1 EndZ=0
  constraints (10):
    c: Coincident(g0,g1)
    c: Coincident(g1,g2)
    c: Coincident(g2,g3)
    c: Coincident(g3,g0)
    c: Vertical(g0)
    c: Vertical(g2)
    c: Horizontal(g1)
    c: Horizontal(g3)
    c: Coincident(g0,g-7)
    c: Coincident(g1,g-4)
FEATURE [PartDesign::Pad] Pad020
  BaseFeature = -> Pad019
  Direction = (0,-1,2e-16)
  Length = 10
  Length2 = 10
  Profile = -> Sketch029
  ReferenceAxis = -> Sketch029 [N_Axis]
  Refine = true
  Suppressed = false
  Type = 0
FEATURE [PartDesign::Body] Body001  label="XPlateNew"
  AllowCompound = false
  Group = -> [Sketch007,Pad005,Sketch009,Pad006,Sketch010,Pocket004,Sketch011,Pad007,Sketch012,Sketch013,Pad008,Pad009,Pocket005,Sketch014,Pocket006,Sketch015,Pad010,Pad011,Pocket007,Sketch016,Pocket008,LinearPattern,Sketch021,Pad015,Sketch025,Pad016,Sketch026,Pad017,Sketch027,Pocket010,Pad018,Sketch028,Pad,Sketch,Pad019,Sketch029,Pad020]
  Origin = -> Origin001
  Tip = -> Pad020
